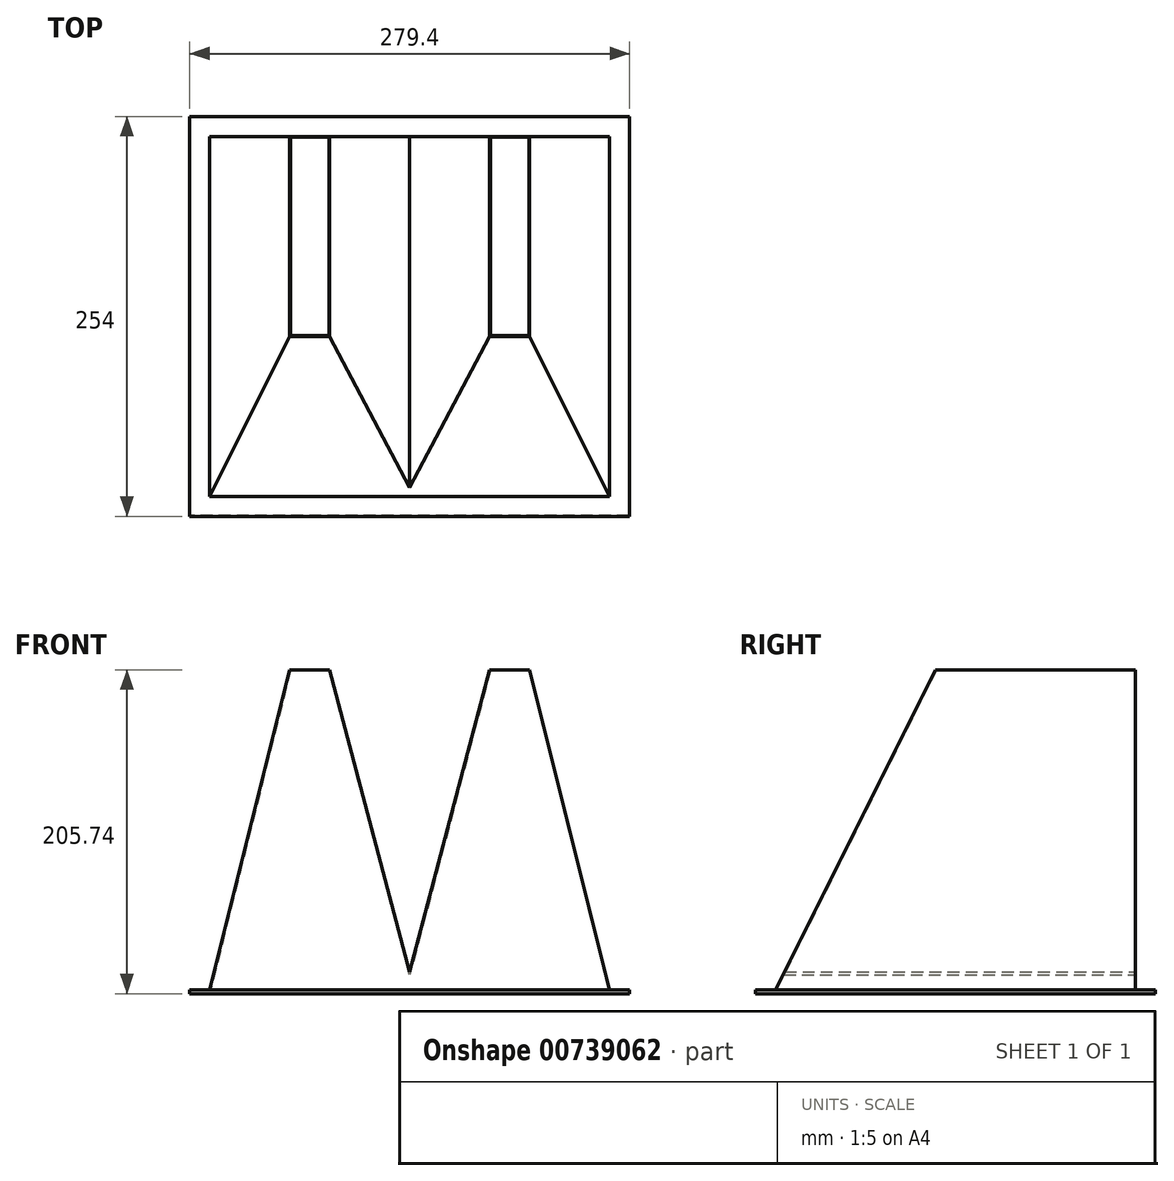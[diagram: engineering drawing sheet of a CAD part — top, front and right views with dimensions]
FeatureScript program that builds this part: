
annotation { "Feature Type Name" : "Feature", "Feature Type Description" : "" }
export const myFeature = defineFeature(function(context is Context, id is Id, definition is map)
    precondition{}
    {
        {
            var Q0;
            Q0=qCreatedBy(makeId("Top.planeOp"),FACE);
            var sketch = newSketch(context, id + "F0", { "sketchPlane" : qUnion([Q0])});
            skLineSegment(sketch, "E0.bottom", {"start": v(-127, -114.3) * mm, "end": v(127, -114.3) * mm});
            skLineSegment(sketch, "E0.top", {"start": v(-127, 114.3) * mm, "end": v(127, 114.3) * mm});
            skLineSegment(sketch, "E0.left", {"start": v(-127, -114.3) * mm, "end": v(-127, 114.3) * mm});
            skLineSegment(sketch, "E0.right", {"start": v(127, -114.3) * mm, "end": v(127, 114.3) * mm});
            skPoint(sketch, "E0.middle", {"position": v(0, 0) * mm});
            skSolve(sketch);
        }
        {
            var Q0;
            Q0=qCreatedBy(makeId("Top.planeOp"),FACE);
            cPlane(context, id + "F1", {"entities" : qUnion([Q0]), "cplaneType" : CPlaneType.OFFSET, "offset" : 203.2 * mm, "width" : 152.4 * mm, "height" : 152.4 * mm});
        }
        {
            var Q0;
            Q0=qCreatedBy(id+"F1.planeOp",FACE);
            var sketch = newSketch(context, id + "F2", { "sketchPlane" : qUnion([Q0])});
            skLineSegment(sketch, "E1.bottom", {"start": v(-76.2, -12.7) * mm, "end": v(-50.8, -12.7) * mm});
            skLineSegment(sketch, "E1.top", {"start": v(-76.2, 12.7) * mm, "end": v(-50.8, 12.7) * mm});
            skLineSegment(sketch, "E1.left", {"start": v(-76.2, -12.7) * mm, "end": v(-76.2, 12.7) * mm});
            skLineSegment(sketch, "E1.right", {"start": v(-50.8, -12.7) * mm, "end": v(-50.8, 12.7) * mm});
            skPoint(sketch, "E1.middle", {"position": v(-63.5, 0) * mm});
            skLineSegment(sketch, "E2", {"start": v(0, 0) * mm, "end": v(-127, 0) * mm, "construction": true});
            skLineSegment(sketch, "E3", {"start": v(0, 0) * mm, "end": v(127, 0) * mm, "construction": true});
            skLineSegment(sketch, "E4.bottom", {"start": v(50.8, 12.7) * mm, "end": v(76.2, 12.7) * mm});
            skLineSegment(sketch, "E4.top", {"start": v(50.8, -12.7) * mm, "end": v(76.2, -12.7) * mm});
            skLineSegment(sketch, "E4.left", {"start": v(50.8, 12.7) * mm, "end": v(50.8, -12.7) * mm});
            skLineSegment(sketch, "E4.right", {"start": v(76.2, 12.7) * mm, "end": v(76.2, -12.7) * mm});
            skPoint(sketch, "E4.middle", {"position": v(63.5, 0) * mm});
            skSolve(sketch);
        }
        {
            var Q0;
            Q0=sQuery(id+"F0.wireOp",VERTEX,"E0.bottom.start");
            var Q1;
            Q1=sQuery(id+"F2.wireOp",VERTEX,"E1.bottom.start");
            var Q2;
            Q2=sQuery(id+"F2.wireOp",VERTEX,"E4.top.end");
            cPlane(context, id + "F3", {"entities" : qUnion([Q0, Q1, Q2]), "cplaneType" : CPlaneType.THREE_POINT, "offset" : 25.4 * mm, "width" : 152.4 * mm, "height" : 152.4 * mm});
        }
        {
            var Q0;
            Q0=qCreatedBy(id+"F3.planeOp",FACE);
            var sketch = newSketch(context, id + "F4", { "sketchPlane" : qUnion([Q0])});
            skLineSegment(sketch, "E5", {"start": v(-127, -51.12) * mm, "end": v(-76.2, 176.07) * mm});
            skLineSegment(sketch, "E6", {"start": v(-50.8, 176.07) * mm, "end": v(0, -38.42) * mm});
            skLineSegment(sketch, "E7", {"start": v(50.8, 176.07) * mm, "end": v(0, -38.42) * mm});
            skLineSegment(sketch, "E8", {"start": v(0, -38.42) * mm, "end": v(0, 181.75) * mm, "construction": true});
            skLineSegment(sketch, "E9.MirrorCS", {"start": v(127, -51.12) * mm, "end": v(76.2, 176.07) * mm});
            skSolve(sketch);
        }
        {
            var Q0;
            Q0=qCreatedBy(makeId("Front.planeOp"),FACE);
            var sketch = newSketch(context, id + "F5", { "sketchPlane" : qUnion([Q0])});
            skLineSegment(sketch, "E10.0", {"start": v(-127, 0) * mm, "end": v(-76.2, 203.2) * mm});
            skLineSegment(sketch, "E10.1", {"start": v(-50.8, 203.2) * mm, "end": v(0, 11.36) * mm});
            skLineSegment(sketch, "E10.2", {"start": v(50.8, 203.2) * mm, "end": v(0, 11.36) * mm});
            skLineSegment(sketch, "E10.3", {"start": v(127, 0) * mm, "end": v(76.2, 203.2) * mm});
            skLineSegment(sketch, "E11", {"start": v(-76.2, 203.2) * mm, "end": v(-50.8, 203.2) * mm});
            skLineSegment(sketch, "E12", {"start": v(50.8, 203.2) * mm, "end": v(76.2, 203.2) * mm});
            skLineSegment(sketch, "E13", {"start": v(127, 0) * mm, "end": v(-127, 0) * mm});
            skSolve(sketch);
        }
        {
            var Q0;
            Q0 = qSketchRegion(id + "F5", true);
            var Q1;
            Q1=sQuery(id+"F4.wireOp",VERTEX,"E5.start");
            var Q2;
            Q2=sQuery(id+"F0.wireOp",VERTEX,"E0.left.end");
            extrude(context, id + "F6", {"entities" : qUnion([Q0]), "endBound" : BoundingType.UP_TO_VERTEX, "depth" : 25.4 * mm, "endBoundEntityVertex" : qUnion([Q1]), "offsetDistance" : 25.4 * mm, "hasSecondDirection" : true, "secondDirectionBound" : SecondDirectionBoundingType.UP_TO_VERTEX, "secondDirectionOppositeDirection" : true, "secondDirectionDepth" : 25.4 * mm, "secondDirectionBoundEntityVertex" : qUnion([Q2])});
        }
        {
            var Q0;
            Q0=qCreatedBy(makeId("Right.planeOp"),FACE);
            var sketch = newSketch(context, id + "F7", { "sketchPlane" : qUnion([Q0])});
            skLineSegment(sketch, "E14.0", {"start": v(-114.3, 0) * mm, "end": v(-114.3, 203.2) * mm});
            skLineSegment(sketch, "E15", {"start": v(-114.3, 203.2) * mm, "end": v(-12.7, 203.2) * mm});
            skLineSegment(sketch, "E16.0", {"start": v(-114.3, 0) * mm, "end": v(-12.7, 203.2) * mm});
            skPoint(sketch, "E17.orphan", {"position": v(0, 203.2) * mm});
            skSolve(sketch);
        }
        {
            var Q0;
            Q0 = qSketchRegion(id + "F7", true);
            extrude(context, id + "F8", {"entities" : qUnion([Q0]), "operationType" : NewBodyOperationType.REMOVE, "endBound" : BoundingType.THROUGH_ALL, "oppositeDirection" : true, "depth" : 25.4 * mm, "offsetDistance" : 25.4 * mm, "hasSecondDirection" : true, "secondDirectionBound" : SecondDirectionBoundingType.THROUGH_ALL, "secondDirectionOppositeDirection" : false, "secondDirectionDepth" : 25.4 * mm});
        }
        {
            var Q0;
            Q0=makeQuery(id+"F6.opExtrude","SWEPT_FACE",FACE,{"disambiguationData":[OSD([sQuery(id+"F5.wireOp",EDGE,"E13")])]});
            var sketch = newSketch(context, id + "F9", { "sketchPlane" : qUnion([Q0])});
            skLineSegment(sketch, "E18.0", {"start": v(139.7, -127) * mm, "end": v(139.7, 127) * mm});
            skLineSegment(sketch, "E18.1", {"start": v(-139.7, -127) * mm, "end": v(139.7, -127) * mm});
            skLineSegment(sketch, "E18.2", {"start": v(-139.7, 127) * mm, "end": v(-139.7, -127) * mm});
            skLineSegment(sketch, "E18.3", {"start": v(139.7, 127) * mm, "end": v(-139.7, 127) * mm});
            skSolve(sketch);
        }
        {
            var Q0;
            Q0 = qSketchRegion(id + "F9", true);
            extrude(context, id + "F10", {"entities" : qUnion([Q0]), "operationType" : NewBodyOperationType.ADD, "depth" : 2.54 * mm, "offsetDistance" : 25.4 * mm});
        }
        {
            var Q0;
            Q0=makeQuery(id+"F10.opExtrude","CAP_FACE",FACE,{"disambiguationData":[OSD([sQuery(id+"F9.wireOp",EDGE,"E18.0"),sQuery(id+"F9.wireOp",EDGE,"E18.1"),sQuery(id+"F9.wireOp",EDGE,"E18.2"),sQuery(id+"F9.wireOp",EDGE,"E18.3")])],"isStart":false});
            var Q1;
            Q1=makeQuery(id+"F6.opExtrude","SWEPT_FACE",FACE,{"disambiguationData":[OSD([sQuery(id+"F5.wireOp",EDGE,"E12")])]});
            var Q2;
            Q2=makeQuery(id+"F6.opExtrude","SWEPT_FACE",FACE,{"disambiguationData":[OSD([sQuery(id+"F5.wireOp",EDGE,"E11")])]});
            shell(context, id + "F11", {"entities" : qUnion([Q0, Q1, Q2]), "thickness" : 0.5 * mm});
        }
    });
